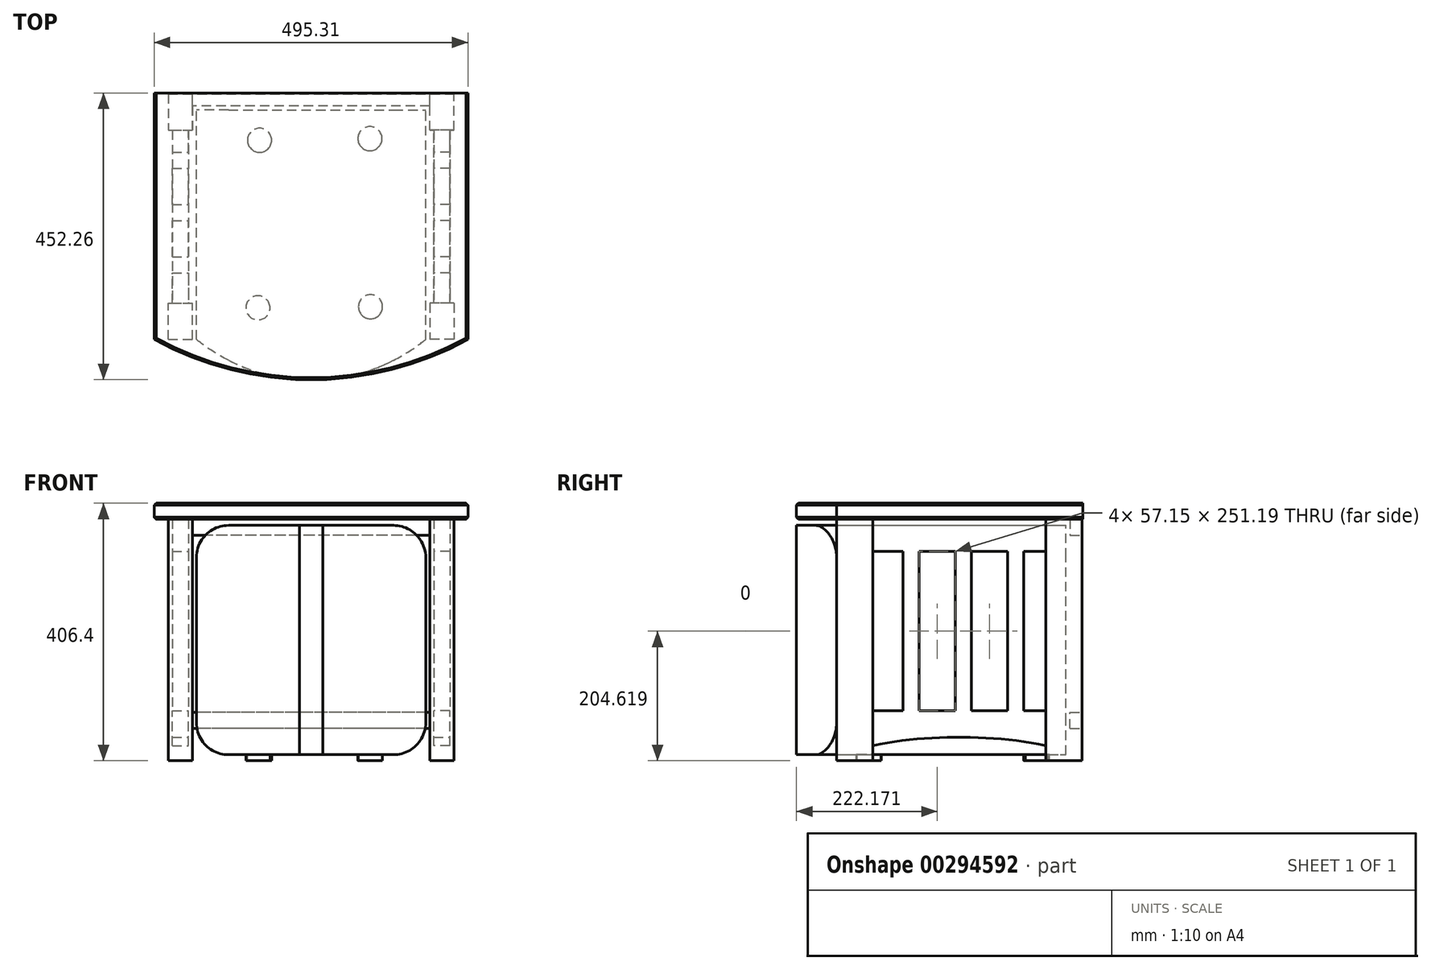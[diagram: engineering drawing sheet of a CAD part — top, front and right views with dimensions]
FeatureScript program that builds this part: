
annotation { "Feature Type Name" : "Feature", "Feature Type Description" : "" }
export const myFeature = defineFeature(function(context is Context, id is Id, definition is map)
    precondition{}
    {
        {
            var Q0;
            Q0=qCreatedBy(makeId("Right.planeOp"),FACE);
            cPlane(context, id + "F0", {"entities" : qUnion([Q0]), "cplaneType" : CPlaneType.OFFSET, "offset" : 6.35 * mm, "oppositeDirection" : true, "width" : 152.4 * mm, "height" : 152.4 * mm});
        }
        {
            var Q0;
            Q0=qCreatedBy(id+"F0.planeOp",FACE);
            cPlane(context, id + "F1", {"entities" : qUnion([Q0]), "cplaneType" : CPlaneType.OFFSET, "offset" : 6.35 * mm, "oppositeDirection" : true, "width" : 152.4 * mm, "height" : 152.4 * mm});
        }
        {
            var Q0;
            Q0=qCreatedBy(makeId("Right.planeOp"),FACE);
            cPlane(context, id + "F2", {"entities" : qUnion([Q0]), "cplaneType" : CPlaneType.OFFSET, "offset" : 180.97 * mm, "width" : 152.4 * mm, "height" : 152.4 * mm});
        }
        {
            var Q0;
            Q0=qCreatedBy(makeId("Front.planeOp"),FACE);
            var sketch = newSketch(context, id + "F3", { "sketchPlane" : qUnion([Q0])});
            skLineSegment(sketch, "E0.bottom", {"start": v(50.8, 0) * mm, "end": v(311.15, 0) * mm});
            skLineSegment(sketch, "E0.top", {"start": v(50.8, 361.95) * mm, "end": v(311.15, 361.95) * mm});
            skLineSegment(sketch, "E0.left", {"start": v(0, 50.8) * mm, "end": v(0, 311.15) * mm});
            skLineSegment(sketch, "E0.right", {"start": v(361.95, 50.8) * mm, "end": v(361.95, 311.15) * mm});
            skPoint(sketch, "E1.visualSharp", {"position": v(0, 0) * mm});
            skArc(sketch, "E1.filletArc", {"start": v(0, 50.8) * mm, "mid": v(14.88, 14.88) * mm, "end": v(50.8, 0) * mm});
            skPoint(sketch, "E2.visualSharp", {"position": v(361.95, 0) * mm});
            skArc(sketch, "E2.filletArc", {"start": v(311.15, 0) * mm, "mid": v(347.07, 14.88) * mm, "end": v(361.95, 50.8) * mm});
            skPoint(sketch, "E3.visualSharp", {"position": v(361.95, 361.95) * mm});
            skArc(sketch, "E3.filletArc", {"start": v(361.95, 311.15) * mm, "mid": v(347.07, 347.07) * mm, "end": v(311.15, 361.95) * mm});
            skPoint(sketch, "E4.visualSharp", {"position": v(0, 361.95) * mm});
            skArc(sketch, "E4.filletArc", {"start": v(50.8, 361.95) * mm, "mid": v(14.88, 347.07) * mm, "end": v(0, 311.15) * mm});
            skSolve(sketch);
        }
        {
            var Q0;
            Q0 = qSketchRegion(id + "F3", true);
            extrude(context, id + "F4", {"entities" : qUnion([Q0]), "depth" : 425.45 * mm});
        }
        {
            var Q0;
            Q0=makeQuery(id+"F4.opExtrude","SWEPT_FACE",FACE,{"disambiguationData":[OSD([sQuery(id+"F3.wireOp",EDGE,"E0.bottom")])]});
            var sketch = newSketch(context, id + "F5", { "sketchPlane" : qUnion([Q0])});
            skCircle(sketch, "E5", {"center": v(97.18, 312.07) * mm, "radius": 19.05 * mm});
            skCircle(sketch, "E6", {"center": v(274.8, 310.3) * mm, "radius": 19.05 * mm});
            skCircle(sketch, "E7", {"center": v(273.93, 45.07) * mm, "radius": 19.05 * mm});
            skCircle(sketch, "E8", {"center": v(99.7, 47.67) * mm, "radius": 19.05 * mm});
            skSolve(sketch);
        }
        {
            var Q0;
            Q0 = qSketchRegion(id + "F5", true);
            extrude(context, id + "F6", {"entities" : qUnion([Q0]), "operationType" : NewBodyOperationType.ADD, "depth" : 9.52 * mm});
        }
        {
            var Q0;
            Q0=makeQuery(id+"F4.opExtrude","SWEPT_FACE",FACE,{"disambiguationData":[OSD([sQuery(id+"F3.wireOp",EDGE,"E0.top")])]});
            var sketch = newSketch(context, id + "F7", { "sketchPlane" : qUnion([Q0])});
            skLineSegment(sketch, "E9.left", {"start": v(0, -425.45) * mm, "end": v(0, -361.95) * mm});
            skLineSegment(sketch, "E9.right", {"start": v(361.95, -425.45) * mm, "end": v(361.95, -361.95) * mm});
            skLineSegment(sketch, "E10.top", {"start": v(0, -444.56) * mm, "end": v(361.95, -444.56) * mm});
            skLineSegment(sketch, "E10.left", {"start": v(0, -425.45) * mm, "end": v(0, -444.56) * mm});
            skLineSegment(sketch, "E10.right", {"start": v(361.95, -425.45) * mm, "end": v(361.95, -444.56) * mm});
            skArc(sketch, "E11", {"start": v(0, -361.95) * mm, "mid": v(180.98, -426.04) * mm, "end": v(361.95, -361.95) * mm});
            skSolve(sketch);
        }
        {
            var Q0;
            Q0 = qSketchRegion(id + "F7", true);
            extrude(context, id + "F8", {"entities" : qUnion([Q0]), "operationType" : NewBodyOperationType.REMOVE, "oppositeDirection" : true, "depth" : 361.95 * mm});
        }
        {
            var Q0;
            Q0=qCreatedBy(id+"F0.planeOp",FACE);
            var sketch = newSketch(context, id + "F9", { "sketchPlane" : qUnion([Q0])});
            skLineSegment(sketch, "E12.top", {"start": v(25.4, 371.48) * mm, "end": v(-31.75, 371.48) * mm});
            skLineSegment(sketch, "E12.left", {"start": v(25.4, -9.54) * mm, "end": v(25.4, 371.48) * mm});
            skLineSegment(sketch, "E12.right", {"start": v(-31.75, -9.54) * mm, "end": v(-31.75, 371.48) * mm});
            skLineSegment(sketch, "E13", {"start": v(-31.75, -9.54) * mm, "end": v(25.4, -9.54) * mm});
            skLineSegment(sketch, "E14.top", {"start": v(-304.8, 371.46) * mm, "end": v(-361.95, 371.46) * mm});
            skLineSegment(sketch, "E14.left", {"start": v(-304.8, -9.54) * mm, "end": v(-304.8, 371.46) * mm});
            skLineSegment(sketch, "E14.right", {"start": v(-361.95, -9.54) * mm, "end": v(-361.95, 371.46) * mm});
            skLineSegment(sketch, "E15", {"start": v(-361.95, -9.54) * mm, "end": v(-304.8, -9.54) * mm});
            skSolve(sketch);
        }
        {
            var Q0;
            Q0 = qSketchRegion(id + "F9", true);
            var Q1;
            Q1 = qSketchRegion(id + "F11", true);
            extrude(context, id + "F10", {"entities" : qUnion([Q0, Q1]), "oppositeDirection" : true, "depth" : 38.1 * mm});
        }
        {
            var Q0;
            Q0=qCreatedBy(id+"F1.planeOp",FACE);
            var sketch = newSketch(context, id + "F11", { "sketchPlane" : qUnion([Q0])});
            skLineSegment(sketch, "E16.0", {"start": v(-31.75, -9.54) * mm, "end": v(-31.75, 69.48) * mm});
            skLineSegment(sketch, "E17.0", {"start": v(-304.8, -9.54) * mm, "end": v(-304.8, 69.48) * mm});
            skLineSegment(sketch, "E18.bottom", {"start": v(-31.75, 371.48) * mm, "end": v(-304.8, 371.48) * mm});
            skLineSegment(sketch, "E18.left", {"start": v(-31.75, 371.48) * mm, "end": v(-31.75, 320.68) * mm});
            skLineSegment(sketch, "E18.right", {"start": v(-304.8, 371.48) * mm, "end": v(-304.8, 320.68) * mm});
            skLineSegment(sketch, "E19", {"start": v(-304.8, 69.48) * mm, "end": v(-304.8, 14.16) * mm});
            skLineSegment(sketch, "E20", {"start": v(-31.75, 14.16) * mm, "end": v(-31.75, 69.48) * mm});
            skPoint(sketch, "E21.1.internal.snap0", {"position": v(-170.21, 14.16) * mm});
            skFitSpline(sketch, "E21", {"points": [v(-31.75, 14.16) * mm, v(-170.21, 27.43) * mm, v(-304.8, 14.16) * mm], "startDerivative": vector(-260.35, 62.24) * mm, "endDerivative": vector(-260.35, -62.24) * mm});
            skLineSegment(sketch, "E22.left", {"start": v(-66.75, 320.68) * mm, "end": v(-66.75, 69.48) * mm});
            skLineSegment(sketch, "E22.right", {"start": v(-92.15, 320.68) * mm, "end": v(-92.15, 69.48) * mm});
            skLineSegment(sketch, "E23.left", {"start": v(-149.3, 320.68) * mm, "end": v(-149.3, 69.48) * mm});
            skLineSegment(sketch, "E23.right", {"start": v(-174.7, 320.68) * mm, "end": v(-174.7, 69.48) * mm});
            skLineSegment(sketch, "E24.left", {"start": v(-231.85, 320.68) * mm, "end": v(-231.85, 69.48) * mm});
            skLineSegment(sketch, "E24.right", {"start": v(-257.25, 320.68) * mm, "end": v(-257.25, 69.48) * mm});
            skLineSegment(sketch, "E25", {"start": v(-170.21, 27.43) * mm, "end": v(-168.28, 396.47) * mm, "construction": true});
            skPoint(sketch, "E25.endSnap0", {"position": v(-168.28, 371.48) * mm});
            skLineSegment(sketch, "E26.trimOffspring", {"start": v(-31.75, 320.68) * mm, "end": v(-31.75, 371.48) * mm});
            skLineSegment(sketch, "E27.trimOffspring", {"start": v(-304.8, 320.68) * mm, "end": v(-304.8, 371.46) * mm});
            skLineSegment(sketch, "E28", {"start": v(-304.8, 69.48) * mm, "end": v(-257.25, 69.48) * mm});
            skLineSegment(sketch, "E29", {"start": v(-231.85, 69.48) * mm, "end": v(-174.7, 69.48) * mm});
            skLineSegment(sketch, "E30", {"start": v(-149.3, 69.48) * mm, "end": v(-92.15, 69.48) * mm});
            skLineSegment(sketch, "E31", {"start": v(-66.75, 69.48) * mm, "end": v(-31.75, 69.48) * mm});
            skLineSegment(sketch, "E32", {"start": v(-31.75, 320.68) * mm, "end": v(-66.75, 320.68) * mm});
            skLineSegment(sketch, "E33", {"start": v(-92.15, 320.68) * mm, "end": v(-149.3, 320.68) * mm});
            skLineSegment(sketch, "E34", {"start": v(-174.7, 320.68) * mm, "end": v(-231.85, 320.68) * mm});
            skLineSegment(sketch, "E35", {"start": v(-257.25, 320.68) * mm, "end": v(-304.8, 320.68) * mm});
            skSolve(sketch);
        }
        {
            var Q0;
            Q0 = qSketchRegion(id + "F11", true);
            var Q1;
            Q1 = qSketchRegion(id + "F15", true);
            extrude(context, id + "F12", {"entities" : qUnion([Q0, Q1]), "operationType" : NewBodyOperationType.ADD, "oppositeDirection" : true, "depth" : 25.4 * mm});
        }
        {
            var Q0;
            Q0=makeQuery(id+"F10.opExtrude","SWEPT_BODY",BODY,{"disambiguationData":[OSD([sQuery(id+"F9.wireOp",EDGE,"E12.top"),sQuery(id+"F9.wireOp",EDGE,"E12.left"),sQuery(id+"F9.wireOp",EDGE,"E12.right"),sQuery(id+"F9.wireOp",EDGE,"E13")])]});
            var Q1;
            Q1=qCreatedBy(id+"F2.planeOp",FACE);
            mirror(context, id + "F13", {"operationType" : NewBodyOperationType.ADD, "entities" : qUnion([Q0]), "mirrorPlane" : qUnion([Q1])});
        }
        {
            var Q0;
            Q0=makeQuery(id+"F10.opExtrude","SWEPT_FACE",FACE,{"disambiguationData":[OSD([sQuery(id+"F9.wireOp",EDGE,"E14.top")])]});
            cPlane(context, id + "F14", {"entities" : qUnion([Q0]), "cplaneType" : CPlaneType.OFFSET, "offset" : 0 * mm, "width" : 152.4 * mm, "height" : 152.4 * mm});
        }
        {
            var Q0;
            Q0=qCreatedBy(id+"F14.planeOp",FACE);
            var sketch = newSketch(context, id + "F15", { "sketchPlane" : qUnion([Q0])});
            skLineSegment(sketch, "E36", {"start": v(180.98, 0) * mm, "end": v(180.98, -78.39) * mm, "construction": true});
            skLineSegment(sketch, "E37", {"start": v(-66.68, 0) * mm, "end": v(-66.68, -361.95) * mm});
            skLineSegment(sketch, "E38", {"start": v(428.63, -361.95) * mm, "end": v(428.63, 0) * mm});
            skPoint(sketch, "E39.0", {"position": v(-44.45, -361.95) * mm});
            skPoint(sketch, "E40.orphan", {"position": v(-66.68, -401.95) * mm});
            skPoint(sketch, "E41.orphan", {"position": v(428.63, -401.95) * mm});
            skPoint(sketch, "E42.0", {"position": v(180.98, -425.45) * mm});
            skArc(sketch, "E43", {"start": v(-66.68, -361.95) * mm, "mid": v(180.98, -425.45) * mm, "end": v(428.63, -361.95) * mm});
            skLineSegment(sketch, "E44", {"start": v(-66.68, 0) * mm, "end": v(-66.68, 26.8) * mm});
            skLineSegment(sketch, "E45", {"start": v(-66.68, 26.8) * mm, "end": v(428.63, 26.8) * mm});
            skLineSegment(sketch, "E46", {"start": v(428.63, 26.8) * mm, "end": v(428.63, 0) * mm});
            skSolve(sketch);
        }
        {
            var Q0;
            Q0 = qSketchRegion(id + "F15", true);
            extrude(context, id + "F16", {"entities" : qUnion([Q0]), "operationType" : NewBodyOperationType.ADD, "depth" : 25.4 * mm});
        }
        {
            var Q0;
            Q0=makeQuery(id+"F16.opExtrude","CAP_EDGE",EDGE,{"disambiguationData":[OSD([sQuery(id+"F15.wireOp",EDGE,"E38")])],"isStart":false});
            var Q1;
            Q1=makeQuery(id+"F16.opExtrude","CAP_EDGE",EDGE,{"disambiguationData":[OSD([sQuery(id+"F15.wireOp",EDGE,"E43")])],"isStart":false});
            var Q2;
            Q2=makeQuery(id+"F16.opExtrude","CAP_EDGE",EDGE,{"disambiguationData":[OSD([sQuery(id+"F15.wireOp",EDGE,"E37")])],"isStart":false});
            var Q3;
            Q3=makeQuery(id+"F16.opExtrude","CAP_EDGE",EDGE,{"disambiguationData":[OSD([sQuery(id+"F15.wireOp",EDGE,"E38")])],"isStart":true});
            var Q4;
            Q4=makeQuery(id+"F16.opExtrude","CAP_EDGE",EDGE,{"disambiguationData":[OSD([sQuery(id+"F15.wireOp",EDGE,"E43")])],"isStart":true});
            var Q5;
            Q5=makeQuery(id+"F16.opExtrude","CAP_EDGE",EDGE,{"disambiguationData":[OSD([sQuery(id+"F15.wireOp",EDGE,"E37")])],"isStart":true});
            chamfer(context, id + "F17", {"entities" : qUnion([Q0, Q1, Q2, Q3, Q4, Q5]), "width" : 3.17 * mm, "tangentPropagation" : true});
        }
        {
            var Q0;
            Q0=makeQuery(id+"F10.opExtrude","SWEPT_FACE",FACE,{"disambiguationData":[OSD([sQuery(id+"F9.wireOp",EDGE,"E12.left")])]});
            var sketch = newSketch(context, id + "F18", { "sketchPlane" : qUnion([Q0])});
            skLineSegment(sketch, "E47.bottom", {"start": v(-368.3, 371.46) * mm, "end": v(6.35, 371.46) * mm});
            skLineSegment(sketch, "E47.top", {"start": v(-368.3, 346.06) * mm, "end": v(6.35, 346.06) * mm});
            skLineSegment(sketch, "E47.left", {"start": v(-368.3, 371.46) * mm, "end": v(-368.3, 346.06) * mm});
            skLineSegment(sketch, "E47.right", {"start": v(6.35, 371.46) * mm, "end": v(6.35, 346.06) * mm});
            skLineSegment(sketch, "E48.bottom", {"start": v(-368.3, 41.26) * mm, "end": v(6.35, 41.26) * mm});
            skLineSegment(sketch, "E48.top", {"start": v(-368.3, 66.66) * mm, "end": v(6.35, 66.66) * mm});
            skLineSegment(sketch, "E48.left", {"start": v(-368.3, 41.26) * mm, "end": v(-368.3, 66.66) * mm});
            skLineSegment(sketch, "E48.right", {"start": v(6.35, 41.26) * mm, "end": v(6.35, 66.66) * mm});
            skSolve(sketch);
        }
        {
            var Q0;
            Q0 = qSketchRegion(id + "F18", true);
            extrude(context, id + "F19", {"entities" : qUnion([Q0]), "operationType" : NewBodyOperationType.ADD, "oppositeDirection" : true, "depth" : 19.05 * mm});
        }
    });
